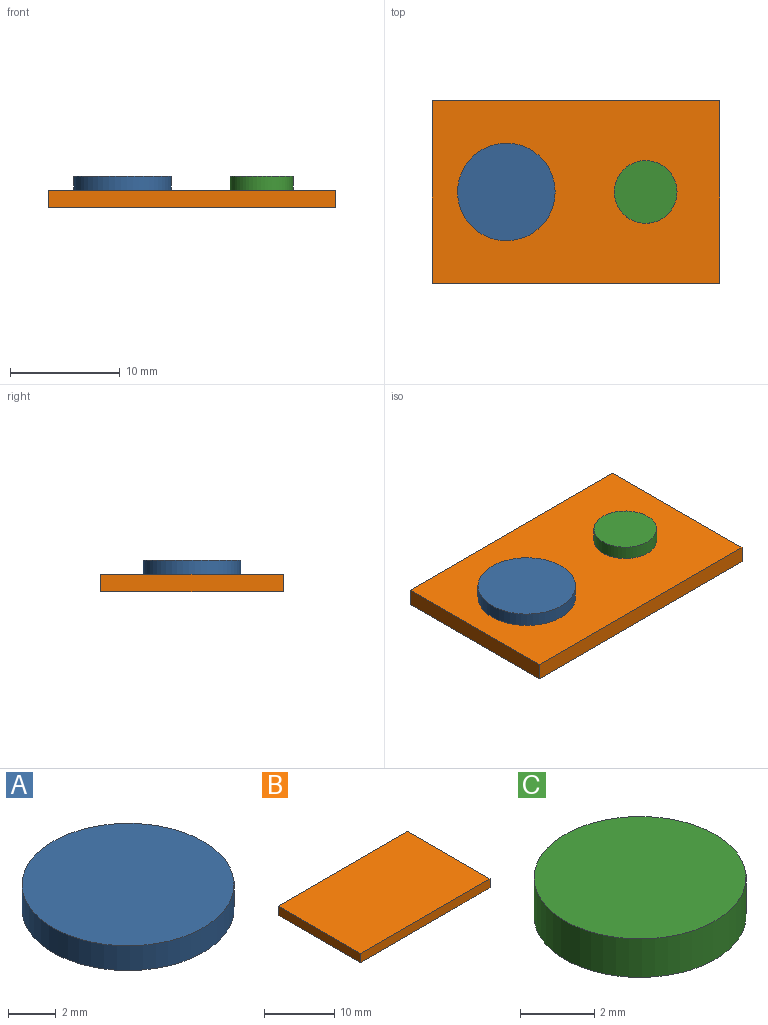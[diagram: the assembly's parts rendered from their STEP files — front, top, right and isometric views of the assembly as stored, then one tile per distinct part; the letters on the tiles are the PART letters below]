
ASSEMBLY  parts=3 mates=2
PART A: 3 faces, bbox 8.9x8.9x1.3 mm
  f0: cylinder r=4.45mm len=8.89mm, axis (0,0,-1), area 35.5mm2, adj f1,f2
  f1: plane 8.89x8.89mm, normal (0,0,1), area 62.1mm2, adj f0
  f2: plane 8.89x8.89mm, normal (0,0,-1), area 62.1mm2, adj f0
PART B: 6 faces, bbox 26.2x16.6x1.6 mm
  f0: plane 26.16x1.59mm, normal (0,1,0), area 41.5mm2, adj f1,f3,f4,f5
  f1: plane 16.64x1.59mm, normal (-1,0,0), area 26.4mm2, adj f0,f2,f4,f5
  f2: plane 26.16x1.59mm, normal (0,-1,0), area 41.5mm2, adj f1,f3,f4,f5
  f3: plane 16.64x1.59mm, normal (1,0,0), area 26.4mm2, adj f0,f2,f4,f5
  f4: plane 26.16x16.64mm, normal (0,0,1), area 435.3mm2, adj f0,f1,f2,f3
  f5: plane 26.16x16.64mm, normal (0,0,-1), area 435.3mm2, adj f0,f1,f2,f3
PART C: 3 faces, bbox 5.7x5.7x1.3 mm
  f0: cylinder r=2.86mm len=5.72mm, axis (0,0,-1), area 22.8mm2, adj f1,f2
  f1: plane 5.72x5.72mm, normal (0,0,1), area 25.7mm2, adj f0
  f2: plane 5.72x5.72mm, normal (0,0,-1), area 25.7mm2, adj f0
PLACE A t=(-68.45,-72.69,12.12)mm
PLACE B t=(-83.33,-51.36,10.54)mm
PLACE C t=(-68.96,-72.69,12.12)mm
MATE fastened B.f4 <-> A.f2  axis (0,0,1) through (-13.48,-2.98,12.12)mm
MATE fastened B.f4 <-> C.f2  axis (0,0,1) through (12.68,-2.98,12.12)mm
